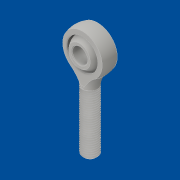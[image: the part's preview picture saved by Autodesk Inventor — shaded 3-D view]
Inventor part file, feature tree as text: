
AUTODESK INVENTOR PART (.ipt)
format: ipt  version: 2016 (Build 200138000, 138)  size: 1,206,784 bytes
history: native  units: in
note: dims shown in document units (in); Inventor stores cm internally (conversion verified against a paired STEP export)
features: other x1, chamfer x1
ambient origin geometry x8: Origin, YZ Plane, XZ Plane, XY Plane, X Axis, Y Axis, Z Axis, Center Point
bodies: Solid1 (feature_tree), Solid2 (feature_tree)
feature tree (2):
  other  "Cut-Extrude2"
  chamfer  "Chamfer1"  [1 undecoded]
note: 1 required parameter value undecoded (feature->parameter linkage not recoverable at this tier; creation-order binding heuristic only, values carry confidence <= 0.55)
